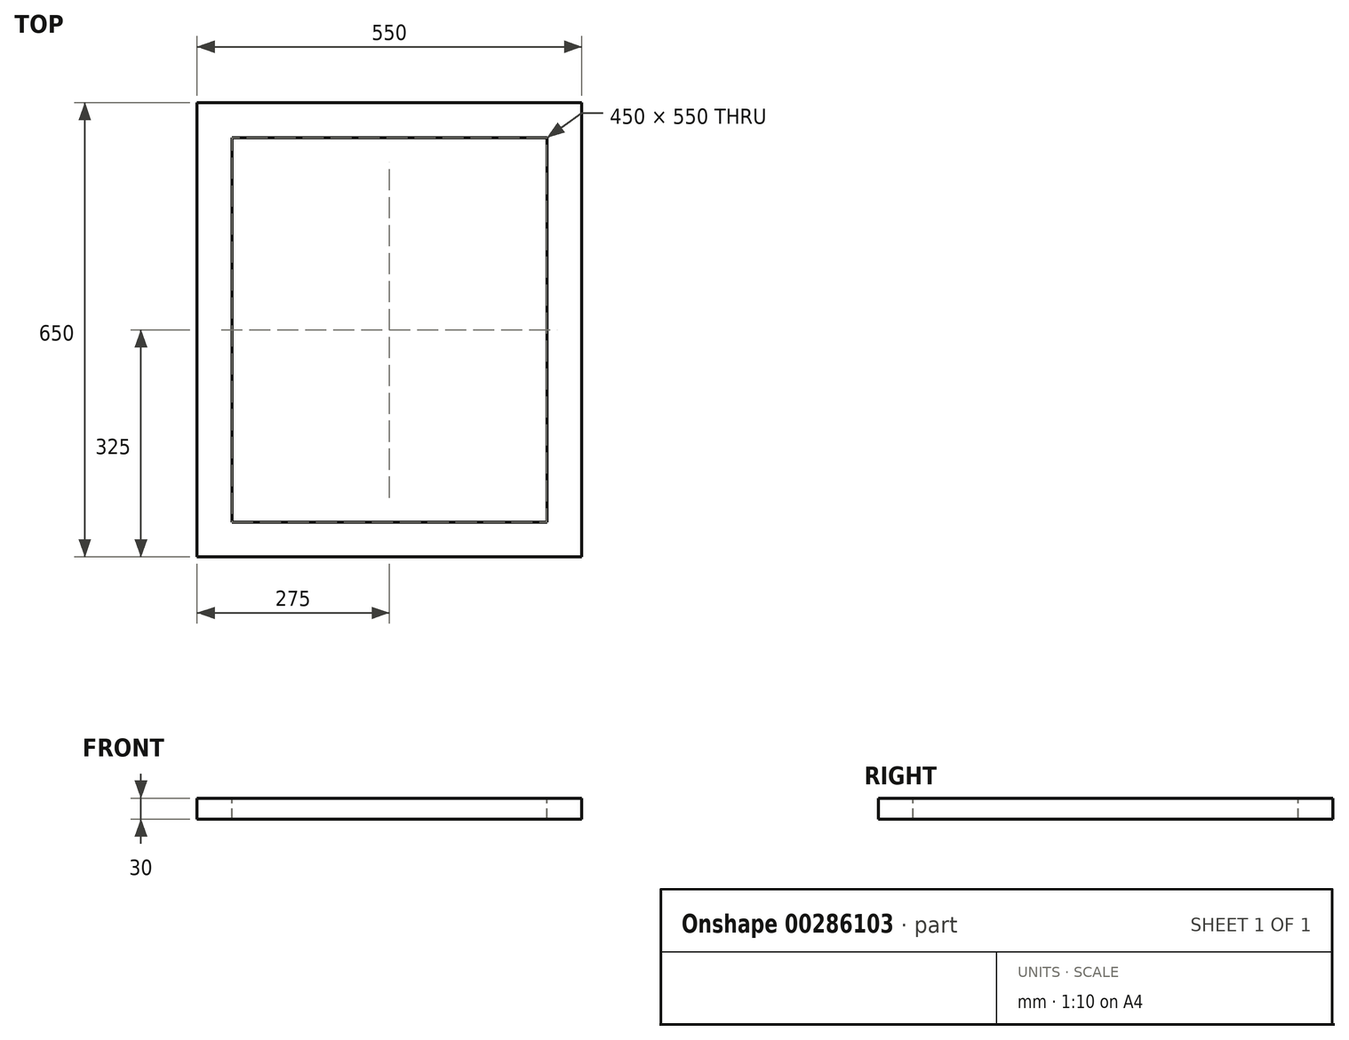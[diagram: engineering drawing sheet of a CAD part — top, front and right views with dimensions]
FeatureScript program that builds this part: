
annotation { "Feature Type Name" : "Feature", "Feature Type Description" : "" }
export const myFeature = defineFeature(function(context is Context, id is Id, definition is map)
    precondition{}
    {
        {
            var Q0;
            Q0=qCreatedBy(makeId("Top.planeOp"),FACE);
            var sketch = newSketch(context, id + "F0", { "sketchPlane" : qUnion([Q0])});
            skLineSegment(sketch, "E0.bottom", {"start": v(-250, 300) * mm, "end": v(250, 300) * mm});
            skLineSegment(sketch, "E0.top", {"start": v(-250, -300) * mm, "end": v(250, -300) * mm});
            skLineSegment(sketch, "E0.left", {"start": v(-250, 300) * mm, "end": v(-250, -300) * mm});
            skLineSegment(sketch, "E0.right", {"start": v(250, 300) * mm, "end": v(250, -300) * mm});
            skPoint(sketch, "E0.middle", {"position": v(0, 0) * mm});
            skSolve(sketch);
        }
        {
            var Q0;
            Q0=qCreatedBy(makeId("Front.planeOp"),FACE);
            var sketch = newSketch(context, id + "F2", { "sketchPlane" : qUnion([Q0])});
            skLineSegment(sketch, "E1.bottom", {"start": v(225, -15) * mm, "end": v(275, -15) * mm});
            skLineSegment(sketch, "E1.top", {"start": v(225, 15) * mm, "end": v(275, 15) * mm});
            skLineSegment(sketch, "E1.left", {"start": v(225, -15) * mm, "end": v(225, 15) * mm});
            skLineSegment(sketch, "E1.right", {"start": v(275, -15) * mm, "end": v(275, 15) * mm});
            skPoint(sketch, "E1.middle", {"position": v(250, 0) * mm});
            skSolve(sketch);
        }
        {
            var Q0;
            Q0=makeQuery(id+"F2.imprint","IMPRINT",FACE,{"disambiguationData":[TD([[makeQuery(id+"F2.imprint","IMPRINT",EDGE,{"derivedFrom":sQuery(id+"F2.wireOp",EDGE,"E1.bottom")}),1.0]])]});
            var Q1;
            Q1=sQuery(id+"F0.wireOp",EDGE,"E0.right");
            var Q2;
            Q2=sQuery(id+"F0.wireOp",EDGE,"E0.top");
            var Q3;
            Q3=sQuery(id+"F0.wireOp",EDGE,"E0.left");
            var Q4;
            Q4=sQuery(id+"F0.wireOp",EDGE,"E0.bottom");
            sweep(context, id + "F1", {"profiles" : qUnion([Q0]), "path" : qUnion([Q1, Q2, Q3, Q4])});
        }
    });
